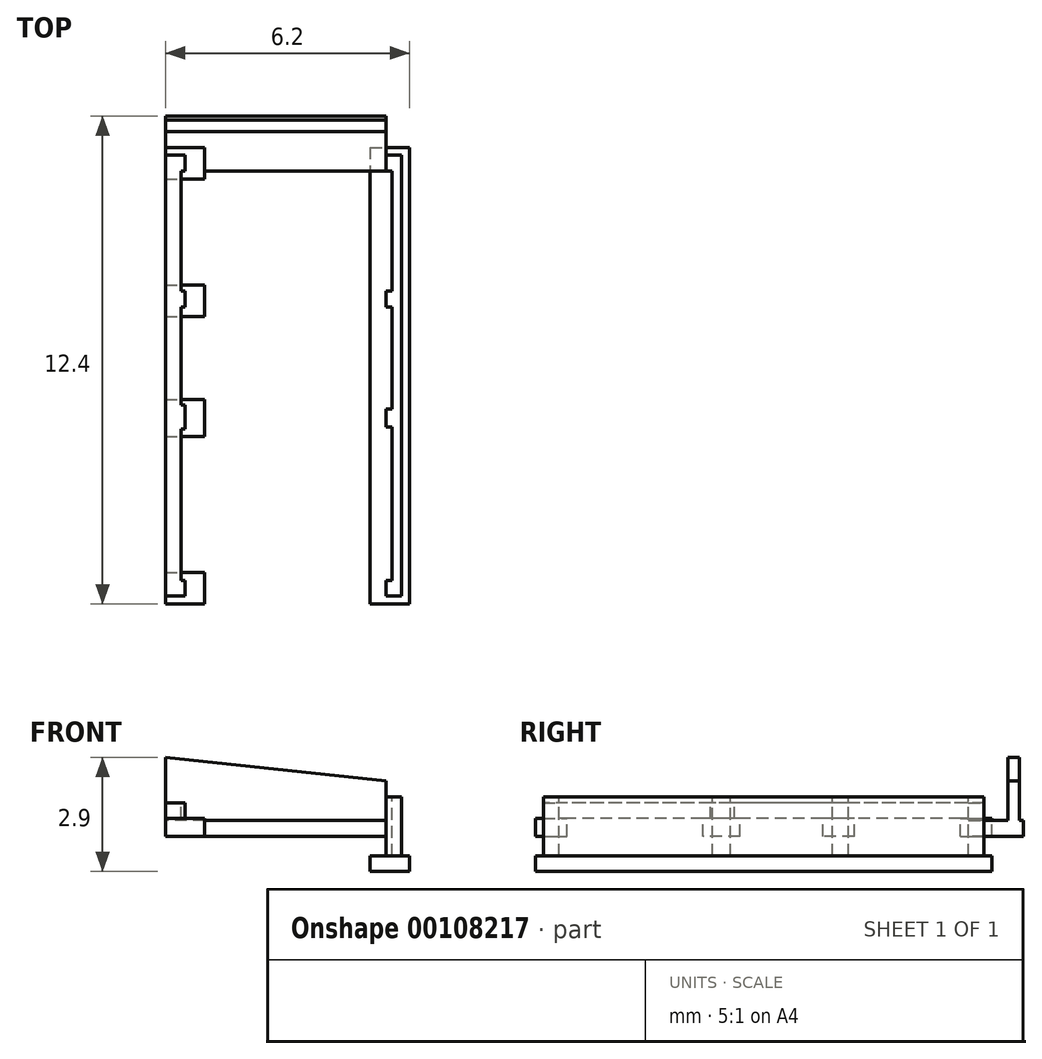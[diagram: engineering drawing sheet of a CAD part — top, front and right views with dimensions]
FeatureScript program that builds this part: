
annotation { "Feature Type Name" : "Feature", "Feature Type Description" : "" }
export const myFeature = defineFeature(function(context is Context, id is Id, definition is map)
    precondition{}
    {
        {
            var Q0;
            Q0=qCreatedBy(makeId("Top.planeOp"),FACE);
            var sketch = newSketch(context, id + "F0", { "sketchPlane" : qUnion([Q0])});
            skLineSegment(sketch, "E0", {"start": v(0, 0) * mm, "end": v(0.5, 0) * mm});
            skLineSegment(sketch, "E1", {"start": v(0.5, 0) * mm, "end": v(0.5, 0.4) * mm});
            skLineSegment(sketch, "E2", {"start": v(0.5, 0.4) * mm, "end": v(0.4, 0.4) * mm});
            skLineSegment(sketch, "E3", {"start": v(0.4, 10.8) * mm, "end": v(0.5, 10.8) * mm});
            skLineSegment(sketch, "E4", {"start": v(0.5, 10.8) * mm, "end": v(0.5, 11.2) * mm});
            skLineSegment(sketch, "E5", {"start": v(0.5, 11.2) * mm, "end": v(0, 11.2) * mm});
            skLineSegment(sketch, "E6", {"start": v(0, 11.2) * mm, "end": v(0, 0) * mm});
            skLineSegment(sketch, "E7", {"start": v(5.6, 0) * mm, "end": v(6, 0) * mm});
            skLineSegment(sketch, "E8", {"start": v(6, 0) * mm, "end": v(6, 11.2) * mm});
            skLineSegment(sketch, "E9", {"start": v(6, 11.2) * mm, "end": v(5.6, 11.2) * mm});
            skLineSegment(sketch, "E10", {"start": v(5.6, 11.2) * mm, "end": v(5.6, 10.8) * mm});
            skLineSegment(sketch, "E11", {"start": v(5.6, 10.8) * mm, "end": v(5.75, 10.8) * mm});
            skLineSegment(sketch, "E12", {"start": v(5.75, 10.8) * mm, "end": v(5.75, 7.75) * mm});
            skLineSegment(sketch, "E13", {"start": v(5.75, 7.75) * mm, "end": v(5.6, 7.75) * mm});
            skLineSegment(sketch, "E14", {"start": v(5.6, 7.75) * mm, "end": v(5.6, 7.35) * mm});
            skLineSegment(sketch, "E15", {"start": v(5.6, 7.35) * mm, "end": v(5.75, 7.35) * mm});
            skLineSegment(sketch, "E16", {"start": v(5.75, 7.35) * mm, "end": v(5.75, 4.75) * mm});
            skLineSegment(sketch, "E17", {"start": v(5.75, 4.75) * mm, "end": v(5.6, 4.75) * mm});
            skLineSegment(sketch, "E18", {"start": v(5.6, 4.75) * mm, "end": v(5.6, 4.3) * mm});
            skLineSegment(sketch, "E19", {"start": v(5.6, 4.3) * mm, "end": v(5.75, 4.3) * mm});
            skLineSegment(sketch, "E20", {"start": v(5.75, 4.3) * mm, "end": v(5.75, 0.4) * mm});
            skLineSegment(sketch, "E21", {"start": v(5.75, 0.4) * mm, "end": v(5.6, 0.4) * mm});
            skLineSegment(sketch, "E22", {"start": v(5.6, 0.4) * mm, "end": v(5.6, 0) * mm});
            skLineSegment(sketch, "E23", {"start": v(0.4, 10.8) * mm, "end": v(0.4, 7.75) * mm});
            skLineSegment(sketch, "E24", {"start": v(0.4, 7.75) * mm, "end": v(0.5, 7.75) * mm});
            skLineSegment(sketch, "E25", {"start": v(0.5, 7.75) * mm, "end": v(0.5, 7.35) * mm});
            skLineSegment(sketch, "E26", {"start": v(0.5, 7.35) * mm, "end": v(0.4, 7.35) * mm});
            skLineSegment(sketch, "E27", {"start": v(0.4, 7.35) * mm, "end": v(0.4, 4.85) * mm});
            skLineSegment(sketch, "E28", {"start": v(0.4, 4.85) * mm, "end": v(0.5, 4.85) * mm});
            skLineSegment(sketch, "E29", {"start": v(0.5, 4.85) * mm, "end": v(0.5, 4.25) * mm});
            skLineSegment(sketch, "E30", {"start": v(0.5, 4.25) * mm, "end": v(0.4, 4.25) * mm});
            skLineSegment(sketch, "E31", {"start": v(0.4, 4.25) * mm, "end": v(0.4, 0.4) * mm});
            skSolve(sketch);
        }
        {
            var Q0;
            Q0=makeQuery(id+"F0.imprint","IMPRINT",FACE,{"disambiguationData":[TD([[makeQuery(id+"F0.imprint","IMPRINT",EDGE,{"derivedFrom":sQuery(id+"F0.wireOp",EDGE,"E0")}),1.0]])]});
            extrude(context, id + "F1", {"entities" : qUnion([Q0]), "oppositeDirection" : true, "depth" : .55 * mm, "hasSecondDirection" : true, "secondDirectionOppositeDirection" : true, "secondDirectionDepth" : .15 * mm});
        }
        {
            var Q0;
            Q0=makeQuery(id+"F0.imprint","IMPRINT",FACE,{"disambiguationData":[TD([[makeQuery(id+"F0.imprint","IMPRINT",EDGE,{"derivedFrom":sQuery(id+"F0.wireOp",EDGE,"E7")}),1.0]])]});
            extrude(context, id + "F2", {"entities" : qUnion([Q0]), "oppositeDirection" : true, "depth" : 1.5 * mm});
        }
        {
            var Q0;
            Q0=qCreatedBy(makeId("Top.planeOp"),FACE);
            var sketch = newSketch(context, id + "F3", { "sketchPlane" : qUnion([Q0])});
            skLineSegment(sketch, "E32.bottom", {"start": v(0, -0.2) * mm, "end": v(1, -0.2) * mm});
            skLineSegment(sketch, "E32.top", {"start": v(0, 0.6) * mm, "end": v(1, 0.6) * mm});
            skLineSegment(sketch, "E32.left", {"start": v(0, -0.2) * mm, "end": v(0, 0.6) * mm});
            skLineSegment(sketch, "E32.right", {"start": v(1, -0.2) * mm, "end": v(1, 0.6) * mm});
            skLineSegment(sketch, "E33.bottom", {"start": v(0, 10.6) * mm, "end": v(1, 10.6) * mm});
            skLineSegment(sketch, "E33.top", {"start": v(0, 11.4) * mm, "end": v(1, 11.4) * mm});
            skLineSegment(sketch, "E33.left", {"start": v(0, 10.6) * mm, "end": v(0, 11.4) * mm});
            skLineSegment(sketch, "E33.right", {"start": v(1, 10.6) * mm, "end": v(1, 11.4) * mm});
            skLineSegment(sketch, "E34.bottom", {"start": v(0, 7.9) * mm, "end": v(1, 7.9) * mm});
            skLineSegment(sketch, "E34.top", {"start": v(0, 7.1) * mm, "end": v(1, 7.1) * mm});
            skLineSegment(sketch, "E34.left", {"start": v(0, 7.9) * mm, "end": v(0, 7.1) * mm});
            skLineSegment(sketch, "E34.right", {"start": v(1, 7.9) * mm, "end": v(1, 7.1) * mm});
            skLineSegment(sketch, "E35.bottom", {"start": v(0, 5) * mm, "end": v(1, 5) * mm});
            skLineSegment(sketch, "E35.top", {"start": v(0, 4.05) * mm, "end": v(1, 4.05) * mm});
            skLineSegment(sketch, "E35.left", {"start": v(0, 5) * mm, "end": v(0, 4.05) * mm});
            skLineSegment(sketch, "E35.right", {"start": v(1, 5) * mm, "end": v(1, 4.05) * mm});
            skLineSegment(sketch, "E36.bottom", {"start": v(5.2, 11.4) * mm, "end": v(6.2, 11.4) * mm});
            skLineSegment(sketch, "E36.top", {"start": v(5.2, -0.2) * mm, "end": v(6.2, -0.2) * mm});
            skLineSegment(sketch, "E36.left", {"start": v(5.2, 11.4) * mm, "end": v(5.2, -0.2) * mm});
            skLineSegment(sketch, "E36.right", {"start": v(6.2, 11.4) * mm, "end": v(6.2, -0.2) * mm});
            skSolve(sketch);
        }
        {
            var Q0;
            Q0=makeQuery(id+"F3.imprint","IMPRINT",FACE,{"disambiguationData":[TD([[makeQuery(id+"F3.imprint","IMPRINT",EDGE,{"derivedFrom":sQuery(id+"F3.wireOp",EDGE,"E32.bottom")}),1.0]])]});
            var Q1;
            Q1=makeQuery(id+"F3.imprint","IMPRINT",FACE,{"disambiguationData":[TD([[makeQuery(id+"F3.imprint","IMPRINT",EDGE,{"derivedFrom":sQuery(id+"F3.wireOp",EDGE,"E35.bottom")}),-1.0]])]});
            var Q2;
            Q2=makeQuery(id+"F3.imprint","IMPRINT",FACE,{"disambiguationData":[TD([[makeQuery(id+"F3.imprint","IMPRINT",EDGE,{"derivedFrom":sQuery(id+"F3.wireOp",EDGE,"E34.bottom")}),-1.0]])]});
            var Q3;
            Q3=makeQuery(id+"F3.imprint","IMPRINT",FACE,{"disambiguationData":[TD([[makeQuery(id+"F3.imprint","IMPRINT",EDGE,{"derivedFrom":sQuery(id+"F3.wireOp",EDGE,"E33.bottom")}),1.0]])]});
            extrude(context, id + "F4", {"entities" : qUnion([Q0, Q1, Q2, Q3]), "operationType" : NewBodyOperationType.ADD, "oppositeDirection" : true, "depth" : 1 * mm, "hasSecondDirection" : true, "secondDirectionOppositeDirection" : true, "secondDirectionDepth" : .55 * mm});
        }
        {
            var Q0;
            Q0=makeQuery(id+"F3.imprint","IMPRINT",FACE,{"disambiguationData":[TD([[makeQuery(id+"F3.imprint","IMPRINT",EDGE,{"derivedFrom":sQuery(id+"F3.wireOp",EDGE,"E36.bottom")}),-1.0]])]});
            extrude(context, id + "F5", {"entities" : qUnion([Q0]), "operationType" : NewBodyOperationType.ADD, "oppositeDirection" : true, "depth" : 1.9 * mm, "hasSecondDirection" : true, "secondDirectionOppositeDirection" : true, "secondDirectionDepth" : 1.5 * mm});
        }
        {
            var Q0;
            Q0=qCreatedBy(makeId("Top.planeOp"),FACE);
            var sketch = newSketch(context, id + "F6", { "sketchPlane" : qUnion([Q0])});
            skLineSegment(sketch, "E37", {"start": v(5.6, 10.8) * mm, "end": v(1, 10.8) * mm});
            skLineSegment(sketch, "E38", {"start": v(1, 10.8) * mm, "end": v(1, 11.4) * mm});
            skLineSegment(sketch, "E39", {"start": v(1, 11.4) * mm, "end": v(0, 11.4) * mm});
            skLineSegment(sketch, "E40", {"start": v(0, 11.4) * mm, "end": v(0, 12.2) * mm});
            skLineSegment(sketch, "E41", {"start": v(0, 12.2) * mm, "end": v(5.6, 12.2) * mm});
            skLineSegment(sketch, "E42", {"start": v(5.6, 12.2) * mm, "end": v(5.6, 10.8) * mm});
            skSolve(sketch);
        }
        {
            var Q0;
            Q0=makeQuery(id+"F6.imprint","IMPRINT",FACE,{"disambiguationData":[TD([[makeQuery(id+"F6.imprint","IMPRINT",EDGE,{"derivedFrom":sQuery(id+"F6.wireOp",EDGE,"E37")}),-1.0]])]});
            extrude(context, id + "F7", {"entities" : qUnion([Q0]), "oppositeDirection" : true, "depth" : 1 * mm, "hasSecondDirection" : true, "secondDirectionOppositeDirection" : true, "secondDirectionDepth" : .6 * mm});
        }
        {
            var Q0;
            Q0=makeQuery(id+"F7.opExtrude","SWEPT_FACE",FACE,{"disambiguationData":[OSD([sQuery(id+"F6.wireOp",EDGE,"E37")])]});
            var sketch = newSketch(context, id + "F8", { "sketchPlane" : qUnion([Q0])});
            skLineSegment(sketch, "E43", {"start": v(5.6, -0.6) * mm, "end": v(5.6, 0.4) * mm});
            skLineSegment(sketch, "E44", {"start": v(5.6, 0.4) * mm, "end": v(0, 1) * mm});
            skLineSegment(sketch, "E45", {"start": v(0, 1) * mm, "end": v(0, -0.6) * mm});
            skLineSegment(sketch, "E46", {"start": v(0, -0.6) * mm, "end": v(5.6, -0.6) * mm});
            skSolve(sketch);
        }
        {
            var Q0;
            {var subQ1=sQuery(id+"F8.wireOp",EDGE,"E43");Q0=makeQuery(id+"F8.imprint","IMPRINT",FACE,{"disambiguationData":[TD([[makeQuery(id+"F8.imprint","IMPRINT",EDGE,{"derivedFrom":subQ1}),1.0]])]});}
            extrude(context, id + "F9", {"entities" : qUnion([Q0]), "operationType" : NewBodyOperationType.ADD, "oppositeDirection" : true, "depth" : 1.3 * mm, "hasSecondDirection" : true, "secondDirectionOppositeDirection" : true, "secondDirectionDepth" : 1 * mm});
        }
    });
